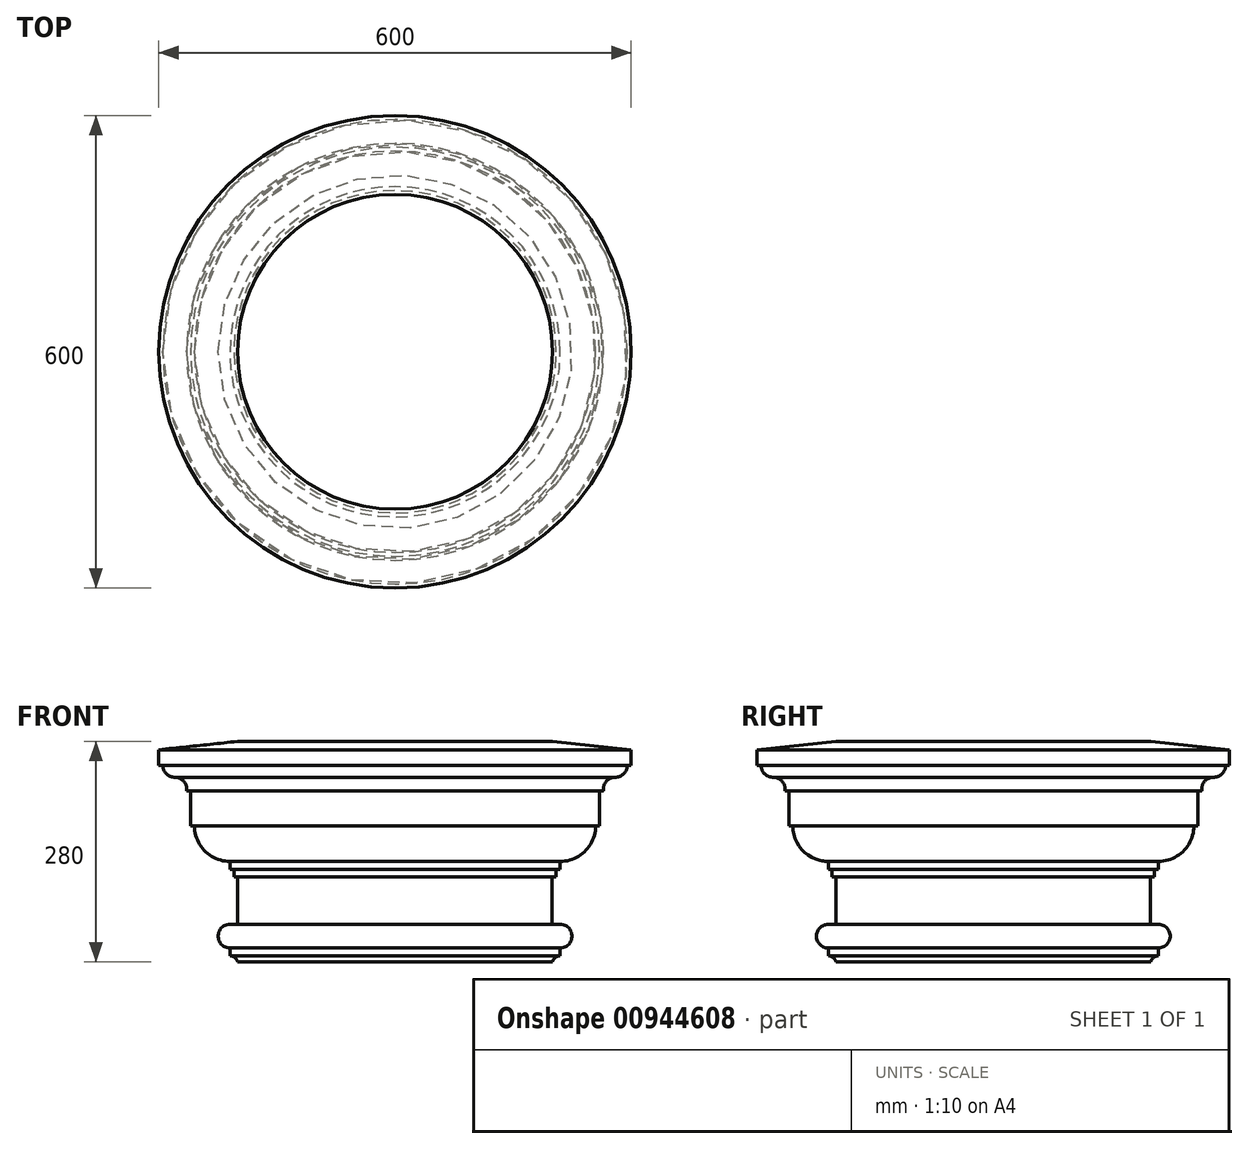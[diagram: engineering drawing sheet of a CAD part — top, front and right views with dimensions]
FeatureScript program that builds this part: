
annotation { "Feature Type Name" : "Feature", "Feature Type Description" : "" }
export const myFeature = defineFeature(function(context is Context, id is Id, definition is map)
    precondition{}
    {
        {
            var Q0;
            Q0=qCreatedBy(makeId("Front.planeOp"),FACE);
            var sketch = newSketch(context, id + "F0", { "sketchPlane" : qUnion([Q0])});
            skLineSegment(sketch, "E0", {"start": v(0, 0) * mm, "end": v(0, 280) * mm});
            skLineSegment(sketch, "E1", {"start": v(0, 280) * mm, "end": v(-200, 280) * mm});
            skLineSegment(sketch, "E2", {"start": v(-200, 280) * mm, "end": v(-300, 269.5) * mm});
            skLineSegment(sketch, "E3", {"start": v(-300, 269.5) * mm, "end": v(-300, 249.5) * mm});
            skLineSegment(sketch, "E4", {"start": v(-300, 249.5) * mm, "end": v(-295, 249.5) * mm});
            skArc(sketch, "E5", {"start": v(-295, 249.5) * mm, "mid": v(-290.54, 238.83) * mm, "end": v(-279.81, 234.5) * mm});
            skArc(sketch, "E6", {"start": v(-279.81, 234.5) * mm, "mid": v(-268.3, 229.33) * mm, "end": v(-264.8, 217.2) * mm});
            skLineSegment(sketch, "E7", {"start": v(-264.8, 217.2) * mm, "end": v(-259.8, 217.2) * mm});
            skLineSegment(sketch, "E8", {"start": v(-259.8, 217.2) * mm, "end": v(-259.8, 172.7) * mm});
            skLineSegment(sketch, "E9", {"start": v(-259.8, 172.7) * mm, "end": v(-254.8, 172.7) * mm});
            skArc(sketch, "E10", {"start": v(-254.8, 172.7) * mm, "mid": v(-241.61, 140.8) * mm, "end": v(-209.72, 127.63) * mm});
            skLineSegment(sketch, "E11", {"start": v(-209.72, 127.63) * mm, "end": v(-209.72, 117.63) * mm});
            skLineSegment(sketch, "E12", {"start": v(-209.72, 117.63) * mm, "end": v(-204.72, 117.63) * mm});
            skLineSegment(sketch, "E13", {"start": v(-204.72, 117.63) * mm, "end": v(-204.72, 107.63) * mm});
            skLineSegment(sketch, "E14", {"start": v(-204.72, 107.63) * mm, "end": v(-199.72, 107.63) * mm});
            skLineSegment(sketch, "E15", {"start": v(-199.72, 107.63) * mm, "end": v(-199.72, 47.63) * mm});
            skLineSegment(sketch, "E16", {"start": v(-199.72, 47.63) * mm, "end": v(-209.72, 47.63) * mm});
            skArc(sketch, "E17", {"start": v(-209.72, 47.63) * mm, "mid": v(-224.72, 32.63) * mm, "end": v(-209.72, 17.63) * mm});
            skLineSegment(sketch, "E18", {"start": v(-209.72, 17.63) * mm, "end": v(-209.72, 7.63) * mm});
            skArc(sketch, "E19", {"start": v(-200, 0) * mm, "mid": v(-203.54, 5.5) * mm, "end": v(-209.72, 7.63) * mm});
            skLineSegment(sketch, "E20", {"start": v(-200, 0) * mm, "end": v(0, 0) * mm});
            skSolve(sketch);
        }
        {
            var Q0;
            Q0=makeQuery(id+"F0.imprint","IMPRINT",FACE,{"disambiguationData":[TD([[makeQuery(id+"F0.imprint","IMPRINT",EDGE,{"derivedFrom":sQuery(id+"F0.wireOp",EDGE,"E0")}),1.0]])]});
            var Q1;
            Q1=sQuery(id+"F0.wireOp",EDGE,"E0");
            revolve(context, id + "F1", {"surfaceOperationType" : NewSurfaceOperationType.NEW, "entities" : qUnion([Q0]), "axis" : qUnion([Q1]), "revolveType" : RevolveType.FULL});
        }
    });
